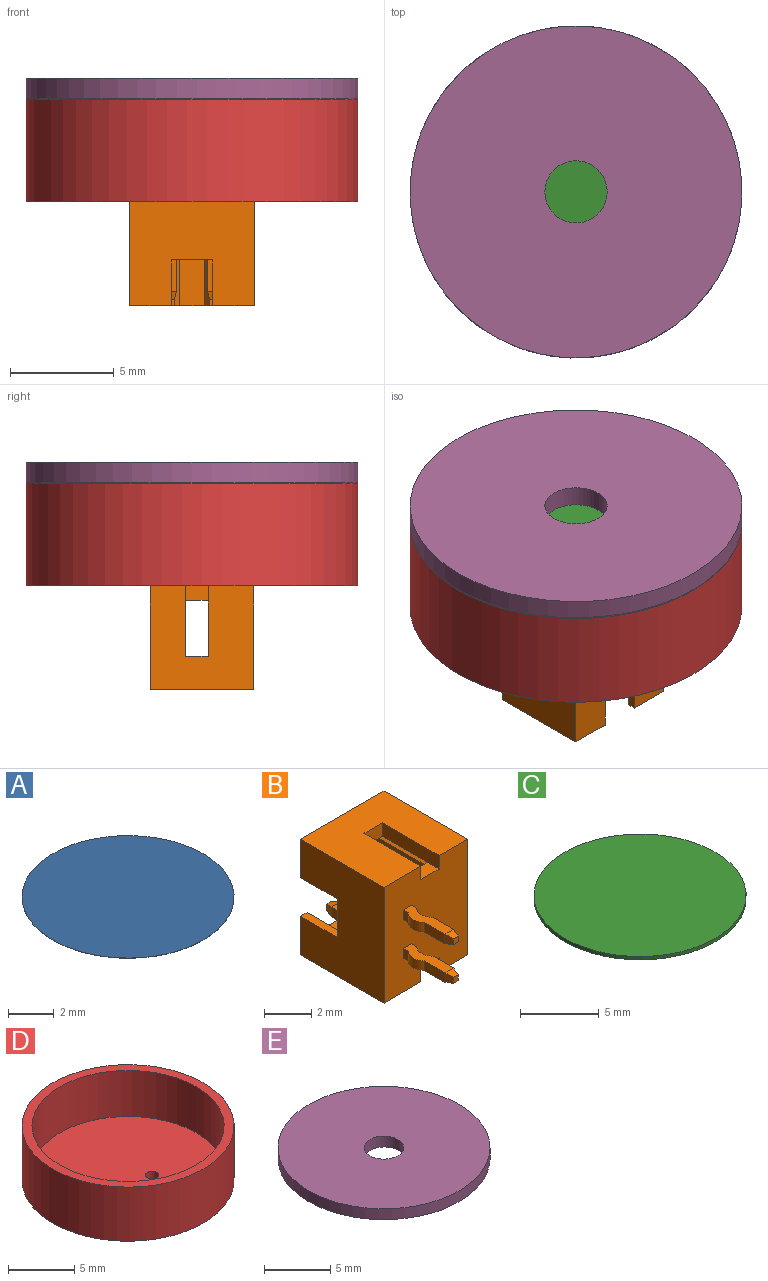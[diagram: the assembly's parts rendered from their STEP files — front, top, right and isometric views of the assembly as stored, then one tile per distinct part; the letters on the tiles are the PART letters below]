
ASSEMBLY  parts=5 mates=4
PART A: 3 faces, bbox 9.3x9.3x0 mm
  f0: cylinder r=4.65mm len=9.3mm, axis (0,0,-1), area 0.3mm2, adj f1,f2
  f1: plane 9.3x9.3mm, normal (0,0,1), area 67.9mm2, adj f0
  f2: plane 9.3x9.3mm, normal (0,0,-1), area 67.9mm2, adj f0
PART B: 74 faces, bbox 5x7.9x6 mm
  f0: plane 4.3x0.35mm, normal (-0.58,0,-0.81), area 1.8mm2, adj f10,f15,f20,f25
  f1: plane 1.1x0.7mm, normal (0,0,-1), area 0.8mm2, adj f3,f25,f27,f38
  f2: plane 2x0.4mm, normal (0,1,0), area 0.8mm2, adj f9,f44,f46,f58
  f3: plane 6x5mm, normal (0,-1,0), area 28mm2, adj f1,f5,f21,f22,f27,f29,f35,f36
  f4: plane 0.5x0.4mm, normal (-0.97,-0.24,0), area 0.2mm2, adj f7,f14,f23,f32
  f5: plane 1.1x0.7mm, normal (0,0,1), area 0.8mm2, adj f3,f21,f25,f38
  f6: plane 1.1x0.7mm, normal (0,-1,0), area 0.8mm2, adj f27,f38,f43,f55
  f7: plane 1.21x0.5mm, normal (-1,0,0), area 0.6mm2, adj f4,f11,f36,f37
  f8: plane 0.5x0.4mm, normal (0.97,-0.24,0), area 0.2mm2, adj f14,f23,f30,f32
  f9: plane 2.2x0.4mm, normal (0,0,-1), area 0.9mm2, adj f2,f15,f44,f46
  f10: plane 4.3x0.3mm, normal (-1,0,0), area 1.3mm2, adj f0,f15,f18,f25
  f11: cylinder r=0.7mm len=0.98mm, axis (0,0,1), area 0.5mm2, adj f7,f36,f37,f39
  f12: plane 4.3x0.3mm, normal (-1,0,0), area 1.3mm2, adj f13,f15,f25,f28
  f13: plane 4.3x0.35mm, normal (-0.58,0,-0.81), area 1.8mm2, adj f12,f15,f17,f25
  f14: plane 0.5x0.4mm, normal (0,-0.24,-0.97), area 0.2mm2, adj f4,f8,f23,f36
  f15: plane 6x5mm, normal (0,1,0), area 10.3mm2, adj f0,f9,f10,f12,f13,f17,f18,f20
  f16: plane 2.7x0.5mm, normal (-1,0,0), area 1.3mm2, adj f19,f40,f53,f54
  f17: plane 4.3x1.2mm, normal (-1,0,0), area 5.2mm2, adj f13,f15,f18,f25
  f18: plane 4.3x0.35mm, normal (-0.58,0,0.81), area 1.8mm2, adj f10,f15,f17,f25
  f19: plane 2.7x0.5mm, normal (0,0,-1), area 1.3mm2, adj f16,f40,f51,f56
  f20: plane 4.3x0.9mm, normal (-1,0,0), area 3.9mm2, adj f0,f15,f25,f43
  f21: plane 3.4x0.7mm, normal (-1,0,0), area 2.4mm2, adj f3,f5,f26,f29,f57
  f22: plane 0.5x0.31mm, normal (1,0,0), area 0.2mm2, adj f3,f31,f36,f37
  f23: plane 0.3x0.3mm, normal (0,-1,0), area 0.1mm2, adj f4,f8,f14,f32
  f24: plane 0.5x0.4mm, normal (0.97,0.24,0), area 0.2mm2, adj f34,f51,f52,f56
  f25: plane 4.6x2.4mm, normal (0,1,0), area 10.7mm2, adj f0,f1,f5,f10,f12,f13,f17,f18
  f26: plane 1.1x0.7mm, normal (0,-1,0), area 0.8mm2, adj f21,f29,f38,f57
  f27: plane 3.4x0.7mm, normal (-1,0,0), area 2.4mm2, adj f1,f3,f6,f43,f55
  f28: plane 4.3x0.35mm, normal (-0.58,0,0.81), area 1.8mm2, adj f12,f15,f25,f33
  f29: plane 5x5mm, normal (0,0,1), area 21.3mm2, adj f3,f15,f21,f26,f35,f38,f46
  f30: plane 1.21x0.5mm, normal (1,0,0), area 0.6mm2, adj f8,f31,f36,f37
  f31: cylinder r=0.7mm len=0.98mm, axis (0,0,1), area 0.5mm2, adj f22,f30,f36,f37
  f32: plane 0.5x0.4mm, normal (0,-0.24,0.97), area 0.2mm2, adj f4,f8,f23,f37
  f33: plane 4.3x0.9mm, normal (-1,0,0), area 3.9mm2, adj f15,f25,f28,f57
  f34: plane 0.3x0.3mm, normal (0,1,0), area 0.1mm2, adj f24,f51,f52,f54
  f35: plane 6x5mm, normal (1,0,0), area 30mm2, adj f3,f15,f29,f55
  f36: plane 2.5x0.7mm, normal (0,0,-1), area 1.2mm2, adj f3,f7,f11,f14,f22,f30,f31,f39
  f37: plane 2.5x0.7mm, normal (0,0,1), area 1.2mm2, adj f3,f7,f11,f22,f30,f31,f32,f39
  f38: plane 6x3.4mm, normal (1,0,0), area 8.9mm2, adj f1,f3,f5,f6,f25,f26,f29,f40
  f39: plane 0.5x0.31mm, normal (-1,0,0), area 0.2mm2, adj f3,f11,f36,f37
  f40: plane 4.6x1.8mm, normal (0,1,0), area 7.8mm2, adj f16,f19,f38,f43,f44,f50,f53,f56
  f41: plane 0.5x0.4mm, normal (-0.97,-0.24,0), area 0.2mm2, adj f47,f68,f69,f73
  f42: cylinder r=0.7mm len=0.98mm, axis (0,0,1), area 0.5mm2, adj f48,f49,f65,f71
  f43: plane 4.3x4.2mm, normal (0,0,1), area 13.5mm2, adj f6,f15,f20,f25,f27,f38,f40,f44
  f44: plane 4.6x3.4mm, normal (1,0,0), area 11.2mm2, adj f2,f9,f15,f40,f43,f57,f58
  f45: plane 0.5x0.4mm, normal (0.97,-0.24,0), area 0.2mm2, adj f47,f49,f68,f69
  f46: plane 6x5mm, normal (-1,0,0), area 25.6mm2, adj f2,f3,f9,f15,f29,f55,f58
  f47: plane 0.5x0.4mm, normal (0,-0.24,0.97), area 0.2mm2, adj f41,f45,f65,f68
  f48: plane 0.5x0.31mm, normal (1,0,0), area 0.2mm2, adj f3,f42,f65,f71
  f49: plane 1.21x0.5mm, normal (1,0,0), area 0.6mm2, adj f42,f45,f65,f71
  f50: plane 2.7x0.5mm, normal (0,0,1), area 1.3mm2, adj f40,f62,f64,f66
  f51: plane 0.5x0.4mm, normal (0,0.24,-0.97), area 0.2mm2, adj f19,f24,f34,f54
  f52: plane 0.5x0.4mm, normal (0,0.24,0.97), area 0.2mm2, adj f24,f34,f53,f54
  f53: plane 2.7x0.5mm, normal (0,0,1), area 1.3mm2, adj f16,f40,f52,f56
  f54: plane 0.5x0.4mm, normal (-0.97,0.24,0), area 0.2mm2, adj f16,f34,f51,f52
  f55: plane 5x5mm, normal (0,0,-1), area 21.3mm2, adj f3,f6,f15,f27,f35,f38,f46
  f56: plane 2.7x0.5mm, normal (1,0,0), area 1.3mm2, adj f19,f24,f40,f53
  f57: plane 4.3x4.2mm, normal (0,0,-1), area 13.5mm2, adj f15,f21,f25,f26,f33,f38,f40,f44
  f58: plane 2.2x0.4mm, normal (0,0,1), area 0.9mm2, adj f2,f15,f44,f46
  f59: plane 0.5x0.4mm, normal (0,0.24,-0.97), area 0.2mm2, adj f60,f61,f63,f67
  f60: plane 0.3x0.3mm, normal (0,1,0), area 0.1mm2, adj f59,f61,f62,f67
  f61: plane 0.5x0.4mm, normal (0.97,0.24,0), area 0.2mm2, adj f59,f60,f62,f64
  f62: plane 0.5x0.4mm, normal (0,0.24,0.97), area 0.2mm2, adj f50,f60,f61,f67
  f63: plane 2.7x0.5mm, normal (0,0,-1), area 1.3mm2, adj f40,f59,f64,f66
  f64: plane 2.7x0.5mm, normal (1,0,0), area 1.3mm2, adj f40,f50,f61,f63
  f65: plane 2.5x0.7mm, normal (0,0,1), area 1.2mm2, adj f3,f42,f47,f48,f49,f70,f72,f73
  f66: plane 2.7x0.5mm, normal (-1,0,0), area 1.3mm2, adj f40,f50,f63,f67
  f67: plane 0.5x0.4mm, normal (-0.97,0.24,0), area 0.2mm2, adj f59,f60,f62,f66
  f68: plane 0.3x0.3mm, normal (0,-1,0), area 0.1mm2, adj f41,f45,f47,f69
  f69: plane 0.5x0.4mm, normal (0,-0.24,-0.97), area 0.2mm2, adj f41,f45,f68,f71
  f70: plane 0.5x0.31mm, normal (-1,0,0), area 0.2mm2, adj f3,f65,f71,f72
  f71: plane 2.5x0.7mm, normal (0,0,-1), area 1.2mm2, adj f3,f42,f48,f49,f69,f70,f72,f73
  f72: cylinder r=0.7mm len=0.98mm, axis (0,0,1), area 0.5mm2, adj f65,f70,f71,f73
  f73: plane 1.21x0.5mm, normal (-1,0,0), area 0.6mm2, adj f41,f65,f71,f72
PART C: 3 faces, bbox 13.5x13.5x0.3 mm
  f0: cylinder r=6.75mm len=13.5mm, axis (0,0,-1), area 11mm2, adj f1,f2
  f1: plane 13.5x13.5mm, normal (0,0,1), area 143.1mm2, adj f0
  f2: plane 13.5x13.5mm, normal (0,0,-1), area 143.1mm2, adj f0
PART D: 7 faces, bbox 16x16x5 mm
  f0: cylinder r=8mm len=16mm, axis (0,0,-1), area 251.3mm2, adj f1,f2
  f1: plane 16x16mm, normal (0,0,1), area 35.9mm2, adj f0,f3
  f2: plane 16x16mm, normal (0,0,-1), area 199.5mm2, adj f0,f5,f6
  f3: cylinder r=7.25mm len=14.5mm, axis (0,0,-1), area 193.6mm2, adj f1,f4
  f4: plane 14.5x14.5mm, normal (0,0,1), area 163.6mm2, adj f3,f5,f6
  f5: cylinder r=0.5mm len=1mm, axis (0,0,-1), area 2.4mm2, adj f2,f4
  f6: cylinder r=0.5mm len=1mm, axis (0,0,-1), area 2.4mm2, adj f2,f4
PART E: 18 faces, bbox 16x16x1.4 mm
  f0: cylinder r=1.5mm len=3mm, axis (0,0,-1), area 9.4mm2, adj f1,f3
  f1: plane 16x16mm, normal (0,0,1), area 194mm2, adj f0,f2
  f2: cylinder r=8mm len=16mm, axis (0,0,-1), area 50.3mm2, adj f1,f3
  f3: plane 16x16mm, normal (0,0,-1), area 189.7mm2, adj f0,f2,f4,f5,f6,f7,f8,f9
  f4: plane 1.56x0.4mm, normal (0,1,0), area 0.6mm2, adj f3,f5,f9,f10
  f5: cylinder r=5.75mm len=0.67mm, axis (0,0,1), area 0.3mm2, adj f3,f4,f6,f10
  f6: plane 0.78x0.4mm, normal (1,0,0), area 0.3mm2, adj f3,f5,f7,f10
  f7: cylinder r=5mm len=2.9mm, axis (0,0,1), area 1.2mm2, adj f3,f6,f8,f10
  f8: plane 0.78x0.4mm, normal (-1,0,0), area 0.3mm2, adj f3,f7,f9,f10
  f9: cylinder r=5.75mm len=0.67mm, axis (0,0,1), area 0.3mm2, adj f3,f4,f8,f10
  f10: plane 2.9x0.91mm, normal (0,0,-1), area 2.1mm2, adj f4,f5,f6,f7,f8,f9
  f11: cylinder r=5.75mm len=0.67mm, axis (0,0,1), area 0.3mm2, adj f3,f12,f16,f17
  f12: plane 1.56x0.4mm, normal (0,-1,0), area 0.6mm2, adj f3,f11,f13,f17
  f13: cylinder r=5.75mm len=0.67mm, axis (0,0,1), area 0.3mm2, adj f3,f12,f14,f17
  f14: plane 0.78x0.4mm, normal (-1,0,0), area 0.3mm2, adj f3,f13,f15,f17
  f15: cylinder r=5mm len=2.9mm, axis (0,0,1), area 1.2mm2, adj f3,f14,f16,f17
  f16: plane 0.78x0.4mm, normal (1,0,0), area 0.3mm2, adj f3,f11,f15,f17
  f17: plane 2.9x0.91mm, normal (0,0,-1), area 2.1mm2, adj f11,f12,f13,f14,f15,f16
PLACE A rot(axis=(1,0,0),180deg) t=(-1.38,-3.97,6.72)mm
PLACE B rot(axis=(-0.58,-0.58,0.58),120deg) t=(-2.82,5.53,1.12)mm
PLACE C rot(axis=(1,0,0),180deg) t=(-1.38,-3.97,6.72)mm
PLACE D t=(-1.38,-3.97,2.18)mm
PLACE E t=(-1.38,-3.97,7.12)mm fixed
MATE fastened A.f0 <-> C.f0  axis (0,0,1) through (-1.38,-3.97,6.46)mm
MATE slider B.f23 <-> D.f5  axis (0,0,1) through (-2.38,-5.55,5.07)mm
MATE slider C.f0 <-> E.f7  axis (0,0,1) through (-1.38,-3.97,6.72)mm
MATE slider D.f0 <-> E.f0  axis (0,0,1) through (-1.38,-3.97,7.18)mm
